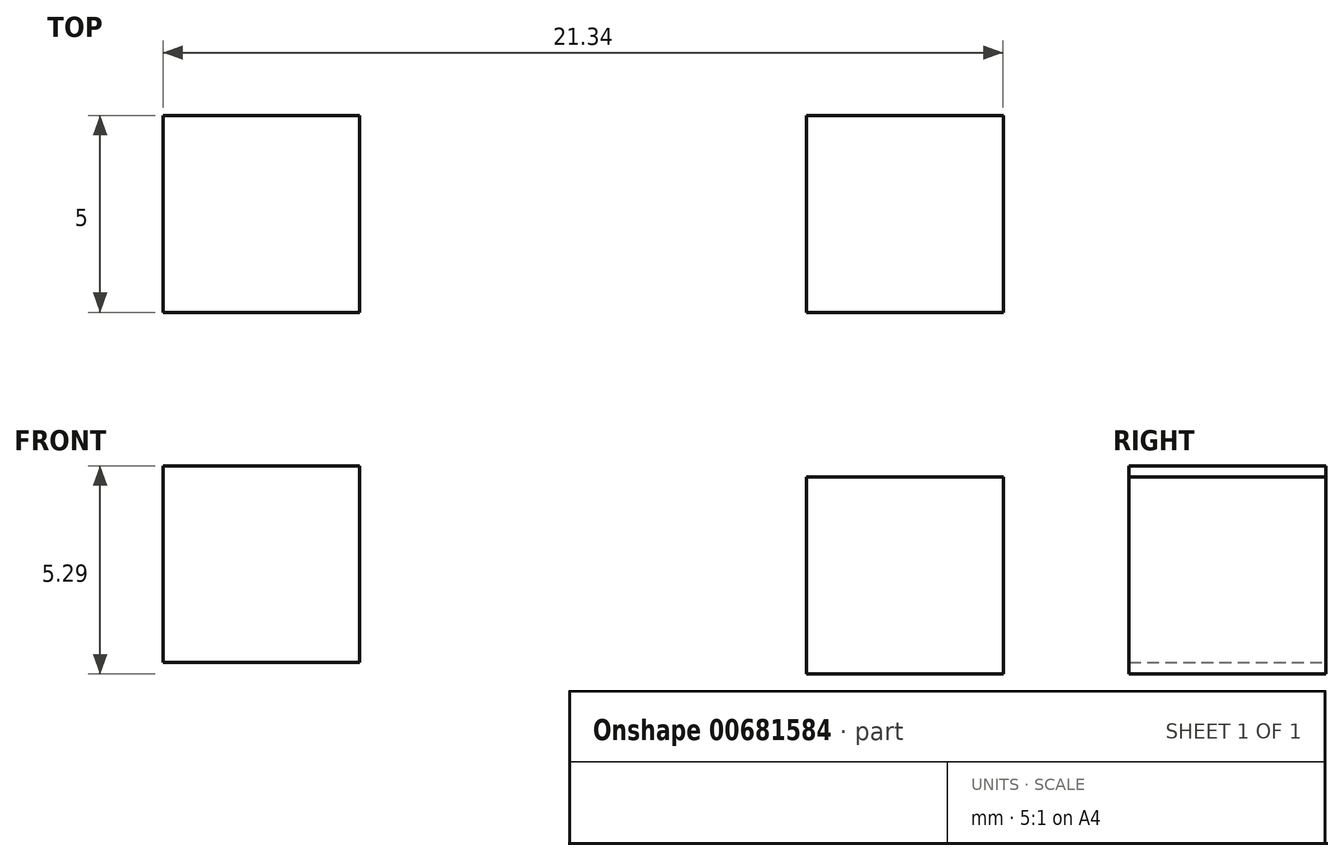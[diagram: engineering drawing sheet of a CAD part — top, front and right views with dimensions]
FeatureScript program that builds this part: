
annotation { "Feature Type Name" : "Feature", "Feature Type Description" : "" }
export const myFeature = defineFeature(function(context is Context, id is Id, definition is map)
    precondition{}
    {
        {
            var Q0;
            Q0=qCreatedBy(makeId("Front.planeOp"),FACE);
            var sketch = newSketch(context, id + "F0", { "sketchPlane" : qUnion([Q0])});
            skLineSegment(sketch, "E0.bottom", {"start": v(-40.4, 25.46) * mm, "end": v(-35.4, 25.46) * mm});
            skLineSegment(sketch, "E0.top", {"start": v(-40.4, 20.46) * mm, "end": v(-35.4, 20.46) * mm});
            skLineSegment(sketch, "E0.left", {"start": v(-40.4, 25.46) * mm, "end": v(-40.4, 20.46) * mm});
            skLineSegment(sketch, "E0.right", {"start": v(-35.4, 25.46) * mm, "end": v(-35.4, 20.46) * mm});
            skLineSegment(sketch, "E1.bottom", {"start": v(-24.06, 25.17) * mm, "end": v(-19.06, 25.17) * mm});
            skLineSegment(sketch, "E1.top", {"start": v(-24.06, 20.17) * mm, "end": v(-19.06, 20.17) * mm});
            skLineSegment(sketch, "E1.left", {"start": v(-24.06, 25.17) * mm, "end": v(-24.06, 20.17) * mm});
            skLineSegment(sketch, "E1.right", {"start": v(-19.06, 25.17) * mm, "end": v(-19.06, 20.17) * mm});
            skSolve(sketch);
        }
        {
            var Q0;
            Q0 = qSketchRegion(id + "F0", true);
            extrude(context, id + "F1", {"entities" : qUnion([Q0]), "depth" : 5 * mm, "offsetDistance" : 25 * mm});
        }
    });
